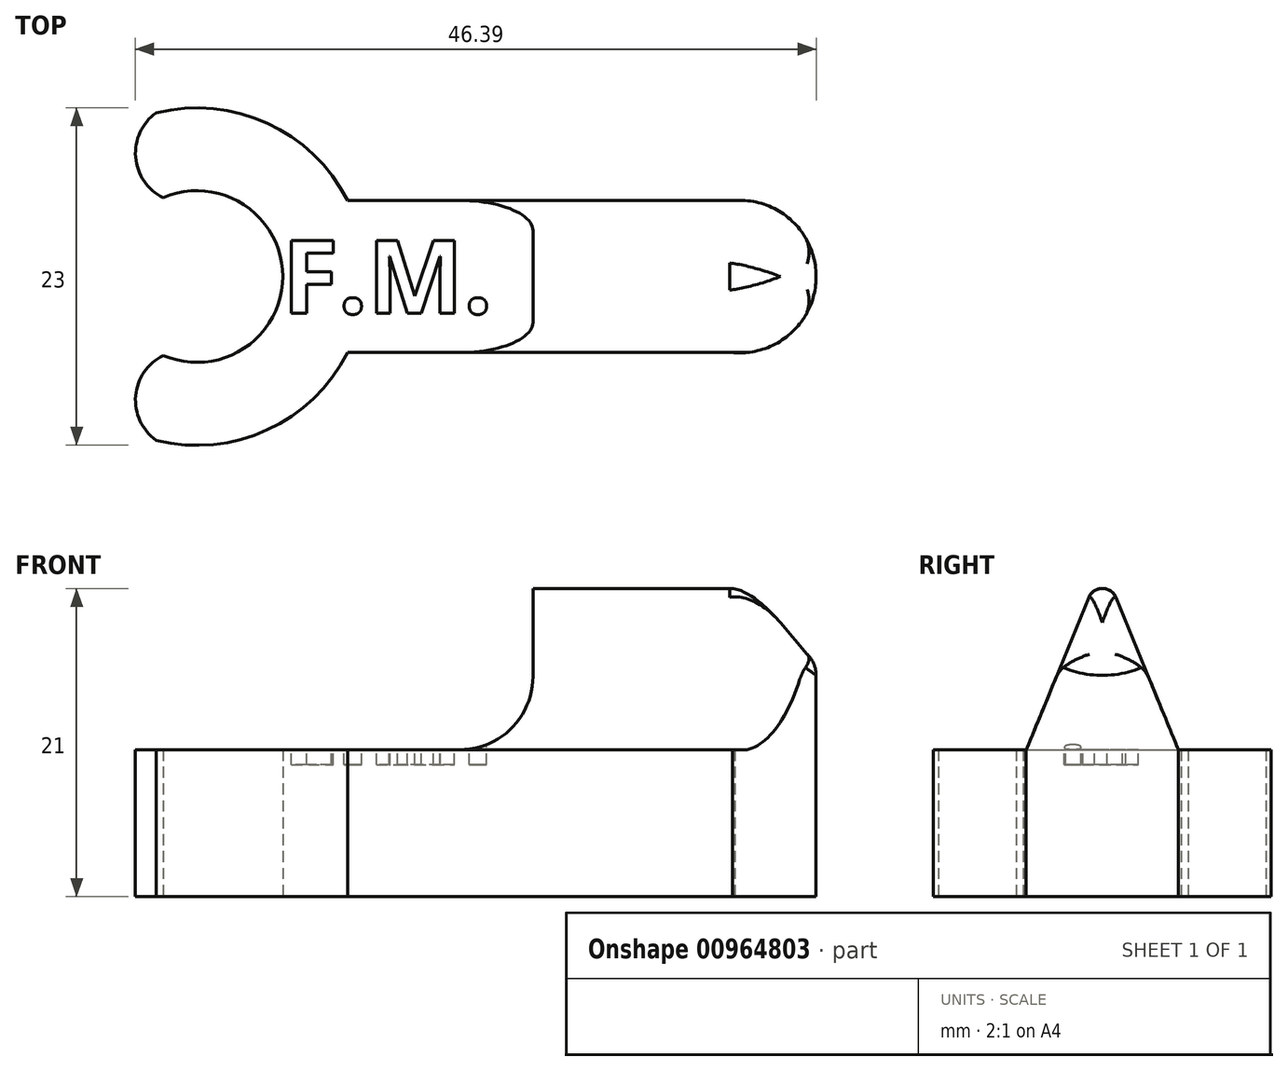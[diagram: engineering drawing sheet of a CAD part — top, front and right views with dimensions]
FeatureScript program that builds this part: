
annotation { "Feature Type Name" : "Feature", "Feature Type Description" : "" }
export const myFeature = defineFeature(function(context is Context, id is Id, definition is map)
    precondition{}
    {
        {
            var Q0;
            Q0=qCreatedBy(makeId("Top.planeOp"),FACE);
            var sketch = newSketch(context, id + "F0", { "sketchPlane" : qUnion([Q0])});
            skArc(sketch, "E0", {"start": v(-2.3, -5.38) * mm, "mid": v(5.85, 0) * mm, "end": v(-2.3, 5.38) * mm});
            skArc(sketch, "E1", {"start": v(10.26, 5.18) * mm, "mid": v(4.79, 10.46) * mm, "end": v(-2.78, 11.16) * mm});
            skArc(sketch, "E2", {"start": v(36.51, -5.17) * mm, "mid": v(42.2, -0.07) * mm, "end": v(36.65, 5.18) * mm});
            skLineSegment(sketch, "E3", {"start": v(37.35, 5.18) * mm, "end": v(10.26, 5.18) * mm});
            skLineSegment(sketch, "E4", {"start": v(37.49, -5.17) * mm, "end": v(10.27, -5.17) * mm});
            skArc(sketch, "E5", {"start": v(-2.78, 11.16) * mm, "mid": v(-4.18, 8.13) * mm, "end": v(-2.3, 5.38) * mm});
            skArc(sketch, "E6.MirrorCS", {"start": v(-2.78, -11.16) * mm, "mid": v(-4.18, -8.13) * mm, "end": v(-2.3, -5.38) * mm});
            skArc(sketch, "E7.trimOffspring", {"start": v(-2.78, -11.16) * mm, "mid": v(4.8, -10.45) * mm, "end": v(10.27, -5.17) * mm});
            skSolve(sketch);
        }
        {
            var Q0;
            Q0 = qSketchRegion(id + "F0", true);
            extrude(context, id + "F1", {"entities" : qUnion([Q0]), "depth" : 10 * mm, "offsetDistance" : 25 * mm});
        }
        {
            var Q0;
            Q0=qCreatedBy(makeId("Right.planeOp"),FACE);
            cPlane(context, id + "F2", {"entities" : qUnion([Q0]), "cplaneType" : CPlaneType.OFFSET, "offset" : 42.9 * mm, "width" : 150 * mm, "height" : 150 * mm});
        }
        {
            var Q0;
            Q0=qCreatedBy(id+"F2.planeOp",FACE);
            var sketch = newSketch(context, id + "F3", { "sketchPlane" : qUnion([Q0])});
            skArc(sketch, "E8", {"start": v(0.93, 20.38) * mm, "mid": v(0, 21) * mm, "end": v(-0.93, 20.38) * mm});
            skLineSegment(sketch, "E9", {"start": v(0.93, 20.38) * mm, "end": v(5.18, 10) * mm});
            skLineSegment(sketch, "E10", {"start": v(-0.93, 20.38) * mm, "end": v(-5.17, 10) * mm});
            skLineSegment(sketch, "E11", {"start": v(-5.17, 10) * mm, "end": v(5.18, 10) * mm});
            skSolve(sketch);
        }
        {
            var Q0;
            Q0 = qSketchRegion(id + "F3", true);
            extrude(context, id + "F4", {"entities" : qUnion([Q0]), "operationType" : NewBodyOperationType.ADD, "oppositeDirection" : true, "depth" : 20 * mm, "offsetDistance" : 25 * mm});
        }
        {
            var Q0;
            Q0=makeQuery(id+"F1.opExtrude","CAP_FACE",FACE,{"disambiguationData":[OSD([sQuery(id+"F0.wireOp",EDGE,"E0"),sQuery(id+"F0.wireOp",EDGE,"E1"),sQuery(id+"F0.wireOp",EDGE,"E2"),sQuery(id+"F0.wireOp",EDGE,"E3"),sQuery(id+"F0.wireOp",EDGE,"E4"),sQuery(id+"F0.wireOp",EDGE,"E5"),sQuery(id+"F0.wireOp",EDGE,"E6.MirrorCS"),sQuery(id+"F0.wireOp",EDGE,"E7.trimOffspring")])],"isStart":true});
            var sketch = newSketch(context, id + "F5", { "sketchPlane" : qUnion([Q0])});
            skArc(sketch, "E12", {"start": v(37.35, -5.18) * mm, "mid": v(42.2, -0.07) * mm, "end": v(37.49, 5.17) * mm});
            skLineSegment(sketch, "E13", {"start": v(37.49, 5.17) * mm, "end": v(44.46, 5.17) * mm});
            skLineSegment(sketch, "E14", {"start": v(44.46, 5.17) * mm, "end": v(44.46, -5.18) * mm});
            skLineSegment(sketch, "E15", {"start": v(44.46, -5.18) * mm, "end": v(37.35, -5.18) * mm});
            skSolve(sketch);
        }
        {
            var Q0;
            Q0 = qSketchRegion(id + "F5", true);
            extrude(context, id + "F6", {"entities" : qUnion([Q0]), "operationType" : NewBodyOperationType.REMOVE, "oppositeDirection" : true, "depth" : 25 * mm, "offsetDistance" : 25 * mm});
        }
        {
            var Q0;
            Q0=makeQuery(id+"F4.opExtrude","CAP_EDGE",EDGE,{"disambiguationData":[OSD([sQuery(id+"F3.wireOp",EDGE,"E11")])],"isStart":false});
            fillet(context, id + "F7", {"entities" : qUnion([Q0]), "radius" : 5 * mm, "tangentPropagation" : true, "allowEdgeOverflow" : false});
        }
        {
            var Q0;
            {var subQ0=sQuery(id+"F0.wireOp",EDGE,"E4");var subQ1=sQuery(id+"F0.wireOp",EDGE,"E1");var subQ2=sQuery(id+"F0.wireOp",EDGE,"E3");var subQ3=sQuery(id+"F0.wireOp",EDGE,"E0");var subQ4=sQuery(id+"F3.wireOp",EDGE,"E10");var subQ5=sQuery(id+"F3.wireOp",EDGE,"E9");var subQ6=sQuery(id+"F0.wireOp",EDGE,"E5");var subQ7=sQuery(id+"F0.wireOp",EDGE,"E6.MirrorCS");var subQ8=sQuery(id+"F0.wireOp",EDGE,"E7.trimOffspring");Q0=makeQuery(id+"F4.boolean.opBoolean","SPLIT",FACE,{"disambiguationData":[TD([makeQuery(id+"F1.opExtrude","SWEPT_FACE",FACE,{"disambiguationData":[OSD([subQ3])]}),makeQuery(id+"F1.opExtrude","SWEPT_FACE",FACE,{"disambiguationData":[OSD([subQ1])]}),makeQuery(id+"F1.opExtrude","SWEPT_FACE",FACE,{"disambiguationData":[OSD([subQ2])]}),makeQuery(id+"F1.opExtrude","SWEPT_FACE",FACE,{"disambiguationData":[OSD([subQ0])]}),makeQuery(id+"F1.opExtrude","SWEPT_FACE",FACE,{"disambiguationData":[OSD([subQ6])]}),makeQuery(id+"F1.opExtrude","SWEPT_FACE",FACE,{"disambiguationData":[OSD([subQ7])]}),makeQuery(id+"F1.opExtrude","SWEPT_FACE",FACE,{"disambiguationData":[OSD([subQ8])]}),makeQuery(id+"F4.opExtrude","CAP_FACE",FACE,{"disambiguationData":[OSD([sQuery(id+"F3.wireOp",EDGE,"E8"),subQ5,subQ4,sQuery(id+"F3.wireOp",EDGE,"E11")])],"isStart":false}),makeQuery(id+"F4.opExtrude","SWEPT_FACE",FACE,{"disambiguationData":[OSD([subQ5])]}),makeQuery(id+"F4.opExtrude","SWEPT_FACE",FACE,{"disambiguationData":[OSD([subQ4])]})])],"derivedFrom":makeQuery(id+"F1.opExtrude","CAP_FACE",FACE,{"disambiguationData":[OSD([subQ3,subQ1,sQuery(id+"F0.wireOp",EDGE,"E2"),subQ2,subQ0,subQ6,subQ7,subQ8])],"isStart":false})});}
            var sketch = newSketch(context, id + "F8", { "sketchPlane" : qUnion([Q0])});
            skText(sketch, "E16", { "text": "F.M.", "fontName": "OpenSans-Bold.ttf"});
            const initialGuessF8  = {"E16": [0.00582, -0.0025, 1, 0, 0.005]};
            skSetInitialGuess(sketch, initialGuessF8);
            skSolve(sketch);
        }
        {
            var Q0;
            Q0 = qSketchRegion(id + "F8", true);
            extrude(context, id + "F9", {"entities" : qUnion([Q0]), "operationType" : NewBodyOperationType.REMOVE, "oppositeDirection" : true, "depth" : 1 * mm, "offsetDistance" : 25 * mm});
        }
        {
            var Q0;
            Q0 = qSketchRegion(id + "F8", true);
            extrude(context, id + "F10", {"entities" : qUnion([Q0]), "operationType" : NewBodyOperationType.REMOVE, "depth" : 25 * mm, "offsetDistance" : 25 * mm});
        }
        {
            var Q0;
            Q0=makeQuery(id+"F1.opExtrude","SWEPT_FACE",FACE,{"disambiguationData":[OSD([sQuery(id+"F0.wireOp",EDGE,"E4")])]});
            var sketch = newSketch(context, id + "F11", { "sketchPlane" : qUnion([Q0])});
            skLineSegment(sketch, "E17", {"start": v(35.87, 23.21) * mm, "end": v(45.78, 11.63) * mm});
            skLineSegment(sketch, "E18", {"start": v(45.78, 11.63) * mm, "end": v(45.78, 24.02) * mm});
            skLineSegment(sketch, "E19", {"start": v(45.78, 24.02) * mm, "end": v(35.87, 23.21) * mm});
            skSolve(sketch);
        }
        {
            var Q0;
            Q0 = qSketchRegion(id + "F11", true);
            extrude(context, id + "F12", {"entities" : qUnion([Q0]), "operationType" : NewBodyOperationType.REMOVE, "oppositeDirection" : true, "depth" : 25 * mm, "offsetDistance" : 25 * mm});
        }
        {
            var Q0;
            Q0=makeQuery(id+"F12.boolean.opBoolean","COPY",FACE,{"derivedFrom":makeQuery(id+"F12.opExtrude","SWEPT_FACE",FACE,{"disambiguationData":[OSD([sQuery(id+"F11.wireOp",EDGE,"E17")])]})});
            fillet(context, id + "F13", {"entities" : qUnion([Q0]), "radius" : 2 * mm, "tangentPropagation" : true, "allowEdgeOverflow" : false});
        }
    });
